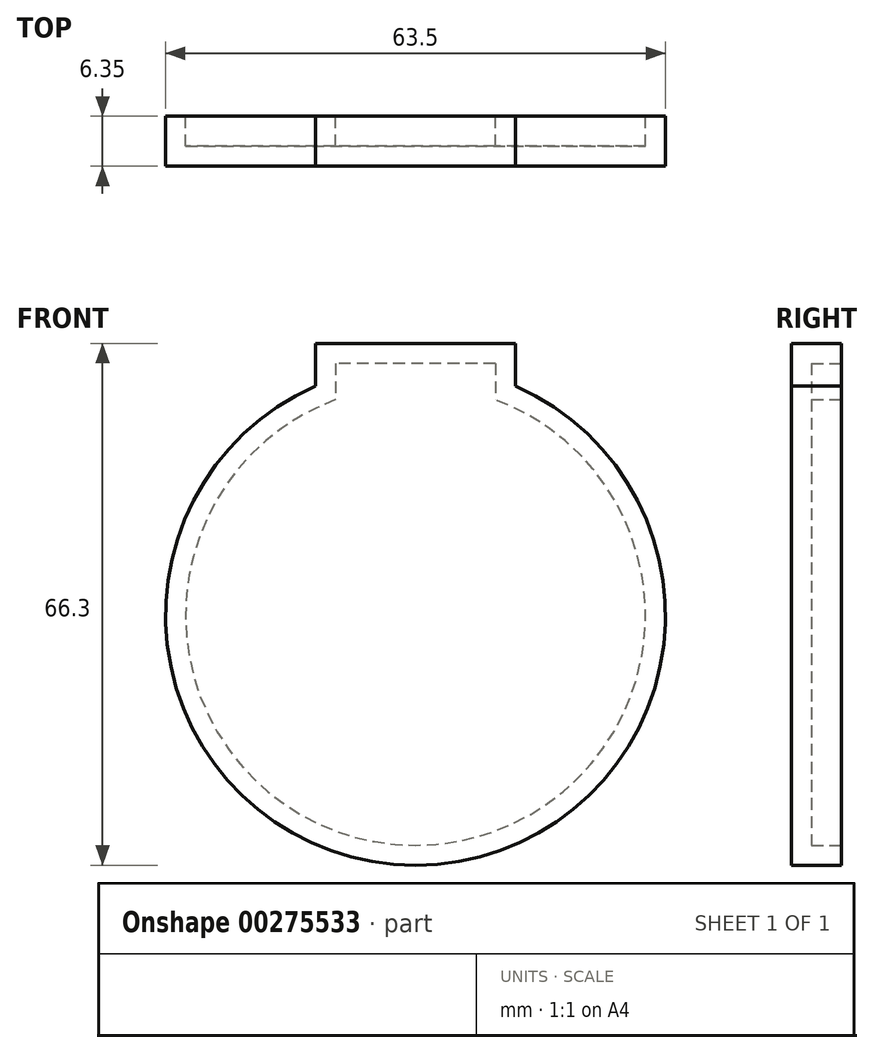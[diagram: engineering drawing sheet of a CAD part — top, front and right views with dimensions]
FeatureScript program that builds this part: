
annotation { "Feature Type Name" : "Feature", "Feature Type Description" : "" }
export const myFeature = defineFeature(function(context is Context, id is Id, definition is map)
    precondition{}
    {
        {
            var Q0;
            Q0=qCreatedBy(makeId("Front.planeOp"),FACE);
            var sketch = newSketch(context, id + "F0", { "sketchPlane" : qUnion([Q0])});
            skCircle(sketch, "E0", {"center": v(0, 0) * mm, "radius": 31.75 * mm});
            skLineSegment(sketch, "E1.bottom", {"start": v(12.7, 34.55) * mm, "end": v(-12.7, 34.55) * mm});
            skLineSegment(sketch, "E1.top", {"start": v(12.7, 28.95) * mm, "end": v(-12.7, 28.95) * mm});
            skLineSegment(sketch, "E1.left", {"start": v(12.7, 34.55) * mm, "end": v(12.7, 28.95) * mm});
            skLineSegment(sketch, "E1.right", {"start": v(-12.7, 34.55) * mm, "end": v(-12.7, 28.95) * mm});
            skPoint(sketch, "E1.middle", {"position": v(0, 31.75) * mm});
            skSolve(sketch);
        }
        {
            var Q0;
            Q0 = qSketchRegion(id + "F0", true);
            extrude(context, id + "F1", {"entities" : qUnion([Q0]), "depth" : 6.35 * mm});
        }
        {
            var Q0;
            Q0=makeQuery(id+"F1.opExtrude","CAP_FACE",FACE,{"disambiguationData":[OSD([sQuery(id+"F0.wireOp",EDGE,"E0"),sQuery(id+"F0.wireOp",EDGE,"E1.bottom"),sQuery(id+"F0.wireOp",EDGE,"E1.top"),sQuery(id+"F0.wireOp",EDGE,"E1.left"),sQuery(id+"F0.wireOp",EDGE,"E1.right")])],"isStart":true});
            shell(context, id + "F2", {"entities" : qUnion([Q0]), "thickness" : 2.54 * mm});
        }
    });
